# Revit family: Шкафы уличные двустенные ШРУД
name_source: partatom
category: Обобщенные модели
units: mm (PartAtom-declared; Revit-internal decimal feet)

## family parameters
Всегда вертикально = Да
Может служить основой для арматурных стержней = Нет
На основе рабочей плоскости = Нет
Общий = Нет
При загрузке вырезать с полостями = Нет
Размер круглого соединителя = Использовать диаметр
Тип детали = Нормальный
Точка расчета площади = Нет

## types (6) — shared parameters
ADSK_URL документации изделия = shru_decl_09_21.pdf (ssd.ru)
ADSK_Единица измерения = шт
ADSK_Завод-изготовитель = АО СВЯЗЬСТРОЙДЕТАЛЬ
ADSK_Размер_Глубина = 345 мм
Материал Каркаса = RAL 7035
Материал болтов = Металл черный
Материал букв = Металл красный
Толщина -4 = -4 мм
Толщина 25 = 25 мм
Толщина 4 = 4 мм
Толщина 5 = 5 мм
zero-valued in all types: Ноль

## per-type parameters (varying)
| type | ADSK_URL страницы изделия | ADSK_Код изделия | ADSK_Масса_Текст | ADSK_Наименование | ADSK_Наименование краткое | ADSK_Размер_Высота | ADSK_Размер_Ширина | Описание |
| ШРУД-600 (60 плинтов ПВТ) | Шкаф распределительный уличный двойной ШРУД-600 укомплектованный ССД ( 120910-00072 ) (ssd.ru) | 120910-00072 | 152 | Шкаф распределительный уличный двойной ШРУД-600  укомплектованный ССД | ШРУД-600 (60 плинтов ПВТ) | 1343 мм | 850 мм | Шкаф распределительный уличный двойной ШРУД-600  укомплектованный ССД |
| ШРУД-1200 (120 плинтов ПВТ) | Шкаф распределительный уличный двойной ШРУД-1200 укомплектованный ССД ( 120910-00071 ) (ssd.ru) | 120910-00071 | 239 | Шкаф распределительный уличный двойной ШРУД-1200 укомплектованный ССД | ШРУД-1200 (120 плинтов ПВТ) | 1900 мм | 850 мм | Шкаф распределительный уличный двойной ШРУД-1200 укомплектованный ССД |
| ШРУД-400 пустой | Шкаф ШРУД-400 без боксов ССД ( 120910-00073 ) (ssd.ru) | 120910-00073 | 92 | Шкаф ШРУД-400 без боксов ССД | ШРУД-400 пустой
ШРУД-400 пустой | 1345 мм | 630 мм | Шкаф ШРУД-400 без боксов ССД |
| ШРУД-600 пустой | Шкаф распределительный уличный двойной ШРУД-600 пустой ССД ( 120910-00066 ) (ssd.ru) | 120910-00066 | 104 | Шкаф распределительный уличный двойной ШРУД-600 пустой ССД | ШРУД-600 пустой | 1345 мм | 850 мм | Шкаф распределительный уличный двойной ШРУД-600 пустой ССД |
| ШРУД-1200 пустой | Шкаф распределительный уличный двойной ШРУД-1200 пустой ССД ( 120910-00067 ) (ssd.ru) | 120910-00067 | 122 | Шкаф распределительный уличный двойной ШРУД-1200 пустой ССД | ШРУД-1200 пустой | 1900 мм | 850 мм | Шкаф распределительный уличный двойной ШРУД-1200 пустой ССД |
| ШРУД-2400 пустой | Шкаф ШРУД-2400 без боксов ССД ( 120910-00069 ) (ssd.ru) | 120910-00069 | 218 | Шкаф ШРУД-2400 без боксов ССД | ШРУД-2400 пустой | 2355 мм | 850 мм | Шкаф ШРУД-2400 без боксов ССД |

## geometry (parser evidence)
native form markers: Blend x2
no freeform markers — native parametric forms only
